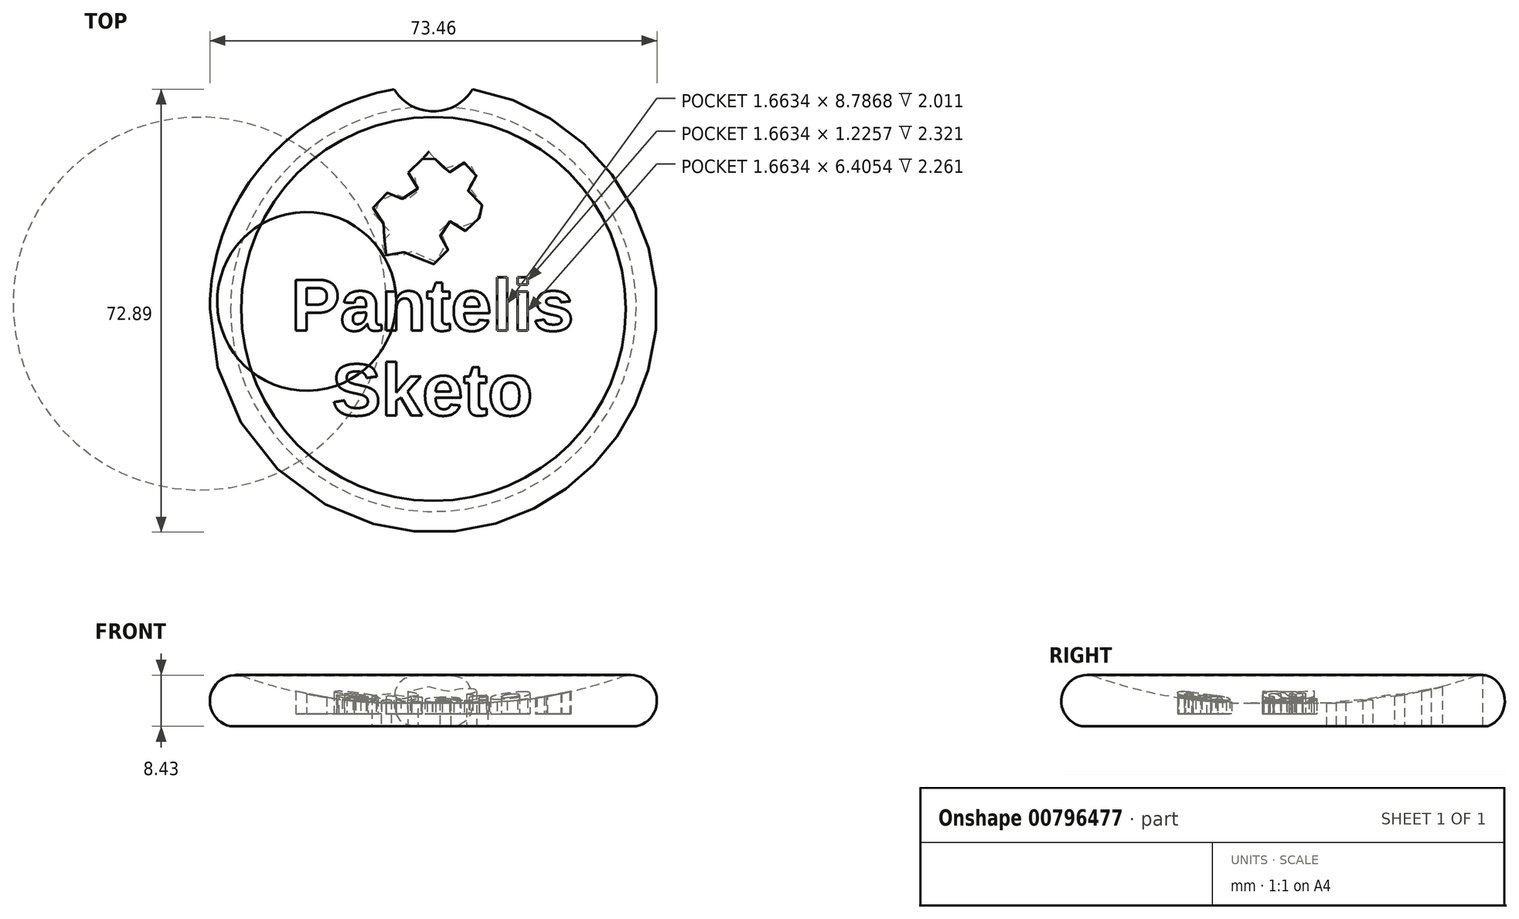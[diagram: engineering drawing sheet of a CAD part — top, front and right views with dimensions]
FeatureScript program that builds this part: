
annotation { "Feature Type Name" : "Feature", "Feature Type Description" : "" }
export const myFeature = defineFeature(function(context is Context, id is Id, definition is map)
    precondition{}
    {
        {
            var Q0;
            Q0=qCreatedBy(makeId("Front.planeOp"),FACE);
            var sketch = newSketch(context, id + "F0", { "sketchPlane" : qUnion([Q0])});
            skLineSegment(sketch, "E0", {"start": v(0, 0) * mm, "end": v(0, 4) * mm});
            skArc(sketch, "E1", {"start": v(-31.59, 8.34) * mm, "mid": v(-16.02, 4.51) * mm, "end": v(0, 4) * mm});
            skArc(sketch, "E2", {"start": v(-31.59, 8.34) * mm, "mid": v(-36.64, 5.05) * mm, "end": v(-33.34, 0) * mm});
            skLineSegment(sketch, "E3", {"start": v(-33.34, 0) * mm, "end": v(0, 0) * mm});
            skSolve(sketch);
        }
        {
            var Q0;
            Q0=makeQuery(id+"F0.imprint","IMPRINT",FACE,{"disambiguationData":[TD([[makeQuery(id+"F0.imprint","IMPRINT",EDGE,{"derivedFrom":sQuery(id+"F0.wireOp",EDGE,"hzpJxE5W-fk26-oNmq-aFCW-cgGpJYh2rfui")}),1.0]])]});
            var Q1;
            Q1=makeQuery(id+"F0.imprint","IMPRINT",FACE,{"disambiguationData":[TD([[makeQuery(id+"F0.imprint","IMPRINT",EDGE,{"derivedFrom":sQuery(id+"F0.wireOp",EDGE,"E0")}),1.0]])]});
            var Q2;
            Q2=sQuery(id+"F0.wireOp",EDGE,"E0");
            revolve(context, id + "F1", {"surfaceOperationType" : NewSurfaceOperationType.NEW, "entities" : qUnion([Q0, Q1]), "axis" : qUnion([Q2]), "revolveType" : RevolveType.FULL});
        }
        {
            var Q0;
            Q0=qCreatedBy(makeId("Top.planeOp"),FACE);
            var sketch = newSketch(context, id + "F2", { "sketchPlane" : qUnion([Q0])});
            skCircle(sketch, "E4", {"center": v(0, 40) * mm, "radius": 7.5 * mm});
            skSolve(sketch);
        }
        {
            var Q0;
            Q0=makeQuery(id+"F2.imprint","IMPRINT",FACE,{"disambiguationData":[TD([[makeQuery(id+"F2.imprint","IMPRINT",EDGE,{"derivedFrom":sQuery(id+"F2.wireOp",EDGE,"E4")}),1.0]])]});
            extrude(context, id + "F3", {"entities" : qUnion([Q0]), "operationType" : NewBodyOperationType.REMOVE, "depth" : 76.2 * mm, "offsetDistance" : 25.4 * mm});
        }
        {
            var Q0;
            Q0=qCreatedBy(makeId("Top.planeOp"),FACE);
            var sketch = newSketch(context, id + "F4", { "sketchPlane" : qUnion([Q0])});
            skText(sketch, "E5", { "text": "Pantelis\n  Sketo", "fontName": "Arimo-Bold.ttf"});
            const initialGuessF4  = {"E5": [-0.02342, -0.00356, 1, 0, 0.00873]};
            skSetInitialGuess(sketch, initialGuessF4);
            skSolve(sketch);
        }
        {
            var Q0;
            Q0 = qSketchRegion(id + "F4", true);
            var Q1;
            Q1=makeQuery(id+"F1.opRevolve","SWEPT_FACE",FACE,{"disambiguationData":[OSD([sQuery(id+"F0.wireOp",EDGE,"E1")])]});
            extrude(context, id + "F5", {"entities" : qUnion([Q0]), "operationType" : NewBodyOperationType.REMOVE, "endBound" : BoundingType.UP_TO_SURFACE, "depth" : 7.87 * mm, "endBoundEntityFace" : qUnion([Q1]), "offsetDistance" : 25.4 * mm, "hasSecondDirection" : true, "secondDirectionOppositeDirection" : true, "secondDirectionDepth" : -2.03 * mm});
        }
        {
            var Q0;
            Q0=qCreatedBy(makeId("Top.planeOp"),FACE);
            var sketch = newSketch(context, id + "F6", { "sketchPlane" : qUnion([Q0])});
            skFitSpline(sketch, "E6", {"points": [v(-4.12, 22.43) * mm, v(-1.06, 25.51) * mm, v(-0.78, 25.87) * mm, v(-0.51, 25.57) * mm, v(2.73, 22.47) * mm, v(3, 22.52) * mm, v(3.16, 22.7) * mm, v(3.18, 22.87) * mm, v(3.37, 23.22) * mm, v(3.67, 23.58) * mm, v(3.95, 23.75) * mm, v(4.22, 23.9) * mm, v(4.58, 24) * mm, v(4.97, 24.07) * mm, v(5.25, 24.05) * mm, v(5.6, 24) * mm, v(5.9, 23.87) * mm, v(6.15, 23.74) * mm, v(6.4, 23.55) * mm, v(6.69, 23.24) * mm, v(6.95, 22.74) * mm, v(7.04, 22.3) * mm, v(7.05, 22.16) * mm, v(7.07, 21.88) * mm, v(7.02, 21.55) * mm, v(6.9, 21.22) * mm, v(6.7, 20.87) * mm, v(6.55, 20.7) * mm, v(6.36, 20.48) * mm, v(6.13, 20.3) * mm, v(5.9, 20.16) * mm, v(5.72, 20.13) * mm, v(5.56, 20.03) * mm, v(5.48, 19.86) * mm, v(5.47, 19.73) * mm, v(5.55, 19.6) * mm, v(5.7, 19.44) * mm, v(8.36, 16.75) * mm, v(8.84, 16.46) * mm, v(8.9, 16.03) * mm, v(8.09, 15.45) * mm, v(7, 14.32) * mm, v(5.63, 12.94) * mm, v(5.43, 12.85) * mm, v(5.25, 12.85) * mm, v(5.08, 12.99) * mm, v(5, 13.21) * mm, v(4.86, 13.5) * mm, v(4.56, 13.86) * mm, v(4.34, 14.05) * mm, v(4, 14.25) * mm, v(3.61, 14.37) * mm, v(3.24, 14.43) * mm, v(2.85, 14.43) * mm, v(2.5, 14.36) * mm, v(2.15, 14.24) * mm, v(1.85, 14.04) * mm, v(1.6, 13.83) * mm, v(1.4, 13.55) * mm, v(1.22, 13.25) * mm, v(1.1, 12.93) * mm, v(1.07, 12.62) * mm, v(1.07, 12.18) * mm, v(1.15, 11.82) * mm, v(1.33, 11.35) * mm, v(1.61, 11.01) * mm, v(1.98, 10.7) * mm, v(2.33, 10.52) * mm, v(2.48, 10.43) * mm, v(2.71, 10.36) * mm, v(2.84, 10.22) * mm, v(2.6, 9.93) * mm, v(-0.4, 6.97) * mm, v(-0.67, 6.86) * mm, v(-0.98, 6.9) * mm, v(-1.38, 7.21) * mm, v(-4.03, 9.88) * mm, v(-4.2, 9.96) * mm, v(-4.25, 10) * mm, v(-4.4, 10.01) * mm, v(-4.56, 9.94) * mm, v(-4.64, 9.7) * mm, v(-4.88, 9.25) * mm, v(-5.32, 8.79) * mm, v(-5.85, 8.52) * mm, v(-6.5, 8.4) * mm, v(-7.07, 8.5) * mm, v(-7.5, 8.66) * mm, v(-7.85, 8.9) * mm, v(-8.08, 9.15) * mm, v(-8.27, 9.42) * mm, v(-8.43, 9.7) * mm, v(-8.5, 9.92) * mm, v(-8.57, 10.26) * mm, v(-8.57, 10.68) * mm, v(-8.5, 11.02) * mm, v(-8.36, 11.36) * mm, v(-8.07, 11.79) * mm, v(-7.88, 11.95) * mm, v(-7.65, 12.16) * mm, v(-7.43, 12.27) * mm, v(-7.16, 12.36) * mm, v(-7.04, 12.44) * mm, v(-6.95, 12.61) * mm, v(-6.94, 12.77) * mm, v(-7.09, 12.99) * mm, v(-7.3, 13.16) * mm, v(-7.68, 13.52) * mm, v(-9.97, 15.85) * mm, v(-10.06, 16.02) * mm, v(-10.12, 16.32) * mm, v(-10.06, 16.5) * mm, v(-9.89, 16.72) * mm, v(-9.35, 17.26) * mm, v(-8.82, 17.82) * mm, v(-7.05, 19.58) * mm, v(-6.75, 19.68) * mm, v(-6.55, 19.51) * mm, v(-6.46, 19.25) * mm, v(-6.3, 18.96) * mm, v(-6.06, 18.67) * mm, v(-5.85, 18.5) * mm, v(-5.53, 18.26) * mm, v(-5.2, 18.14) * mm, v(-4.88, 18.07) * mm, v(-4.42, 18.04) * mm, v(-4.15, 18.1) * mm, v(-3.84, 18.18) * mm, v(-3.63, 18.28) * mm, v(-3.4, 18.42) * mm, v(-3.2, 18.58) * mm, v(-3.02, 18.74) * mm, v(-2.87, 18.96) * mm, v(-2.75, 19.2) * mm, v(-2.65, 19.43) * mm, v(-2.56, 19.74) * mm, v(-2.53, 20.05) * mm, v(-2.55, 20.5) * mm, v(-2.67, 20.82) * mm, v(-2.8, 21.1) * mm, v(-2.9, 21.32) * mm, v(-3.1, 21.53) * mm, v(-3.3, 21.74) * mm, v(-3.5, 21.87) * mm, v(-3.68, 21.96) * mm, v(-3.83, 22.01) * mm, v(-3.98, 22.06) * mm, v(-4.14, 22.15) * mm, v(-4.2, 22.29) * mm, v(-4.12, 22.43) * mm]});
            skSolve(sketch);
        }
        {
            var Q0;
            Q0 = qSketchRegion(id + "F6", true);
            extrude(context, id + "F7", {"entities" : qUnion([Q0]), "operationType" : NewBodyOperationType.REMOVE, "endBound" : BoundingType.SYMMETRIC, "depth" : 50.8 * mm, "offsetDistance" : 25.4 * mm});
        }
    });
